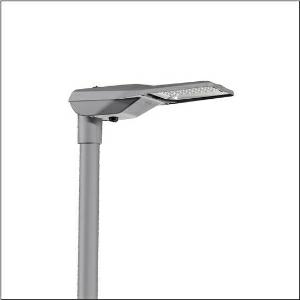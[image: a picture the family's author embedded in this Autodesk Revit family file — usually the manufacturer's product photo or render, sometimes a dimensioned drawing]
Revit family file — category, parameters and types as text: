
# Revit family: streetlight_sl_21_mini___p1_0a_5xe2a33t08gb_80ca
name_source: partatom
category: Lighting Fixtures
units: mm (PartAtom-declared; Revit-internal decimal feet)

## family parameters
Cut with Voids When Loaded = No
Host = Face
Light Source = No
Part Type = Normal
Room Calculation Point = No
Round Connector Dimension = Use Diameter
Shared = No

## types (1)
- --- (1 x LED, 5940 lm, 40.4 W, 3000K)
    Apparent Load = 40 VA
    CIE Flux Codes = 21 50 90 100 100
    Color Rendering = 70
    Color Temperature = 3000K
    Default Elevation = 1800 mm
    Description = Streetlight SL 21 mini, mast luminaire, primary light control with lens, of PMMA, primary optical cover: cover, of toughened safety glass, transparent, light distribution: P1.0a, light emission: direct distribution, primary light characteristic: asymmetric, installation type: side-entry, post-top, LED, High Power LED, rated luminous flux: 5.940lm, luminous efficacy: 147lm/W, light colour: 730, colour temperature: 3000K, control gear: D4i, control: overheat protection, constant luminous flux control, time-dependent luminous flux control, flexible luminous flux parameterisation, pre-setting: logarithmic dimming characteristic, mains connection: 220..240V, AC, 50/60Hz, start of lifetime: 40W, end of service life: 41W, reduction: 19W, luminaire housing, of diecast aluminium, powder-coated, Siteco® metallic grey (DB 702S), corrosivity category C5 mid according to DIN EN ISO 12944, please order mast flange separately, inclination adjustable: 0°, 5°, 10°, 15°, sealing non-destructively replaceable, multi-level sealing system, length: 628mm, width: 235mm, height: 110mm, mast flange for spigot size: 42mm (side-entry): 5XC10008XM4, 60/48mm (side-entry/post-top): 5XC10108XM2, 76/60mm (side-entry/post-top): 5XC10108XM1, mounting height: 4..8m, Smart Interface below and above, protection rating (complete): IP66, insulation class (complete): insulation class II (safety insulation), certification: CE, ENEC, ENEC+, VDE, impact resistance: IK10, permissible operating ambient temperature for outdoor applications: -40..+50°C, standard-compliant lighting for roads and squares, packaging unit: 1 piece

Light Distribution: P1.0a
    Height = 110 mm
    Lamp = 1 x LED
    Lamp Light Flux = 5940 lm
    Lamp Power = 40.4 W
    Lamp count = 1
    Length = 625 mm
    Luminous efficacy = 147 lm/W
    Manufacturer = Siteco
    ModVariant = No
    Model = 5XE2A33T08GB
    Number of Poles = 1
    OnlyDefault = Yes
    Power Factor = 1
    Product Name = Streetlight SL 21 mini | P1.0a
    Product group = mast luminaire | pylon top
    ProductGroupID = 6100
    Protection Class = Protection class II
    Protection Degree = IP 66
    RLX_Detail_Level = 1
    RLX_Emergency_Light_Flux = 0 lm
    RLX_Emergency_Type = 0
    RLX_Emergency_Type_DB = No
    RlxData = <blob elided: 37489 chars, md5=e274b11b>
    Socket = socket
    Standby Power = 0 W
    System Light Flux = 5940 lm
    System Power = 40 W
    Type Comments = factory setting: luminous flux: 100 % | dim-lin: 254 | 812 mA
    Type Image = l_1003514.jpg
    URL = http://relux.com
    VarID = @adj_186552
    Voltage = 0 V
    Weight = 0.00 kg
    Width = 234 mm

## geometry (parser evidence)
native form markers: Blend x4, Sweep x8
no freeform markers — native parametric forms only
